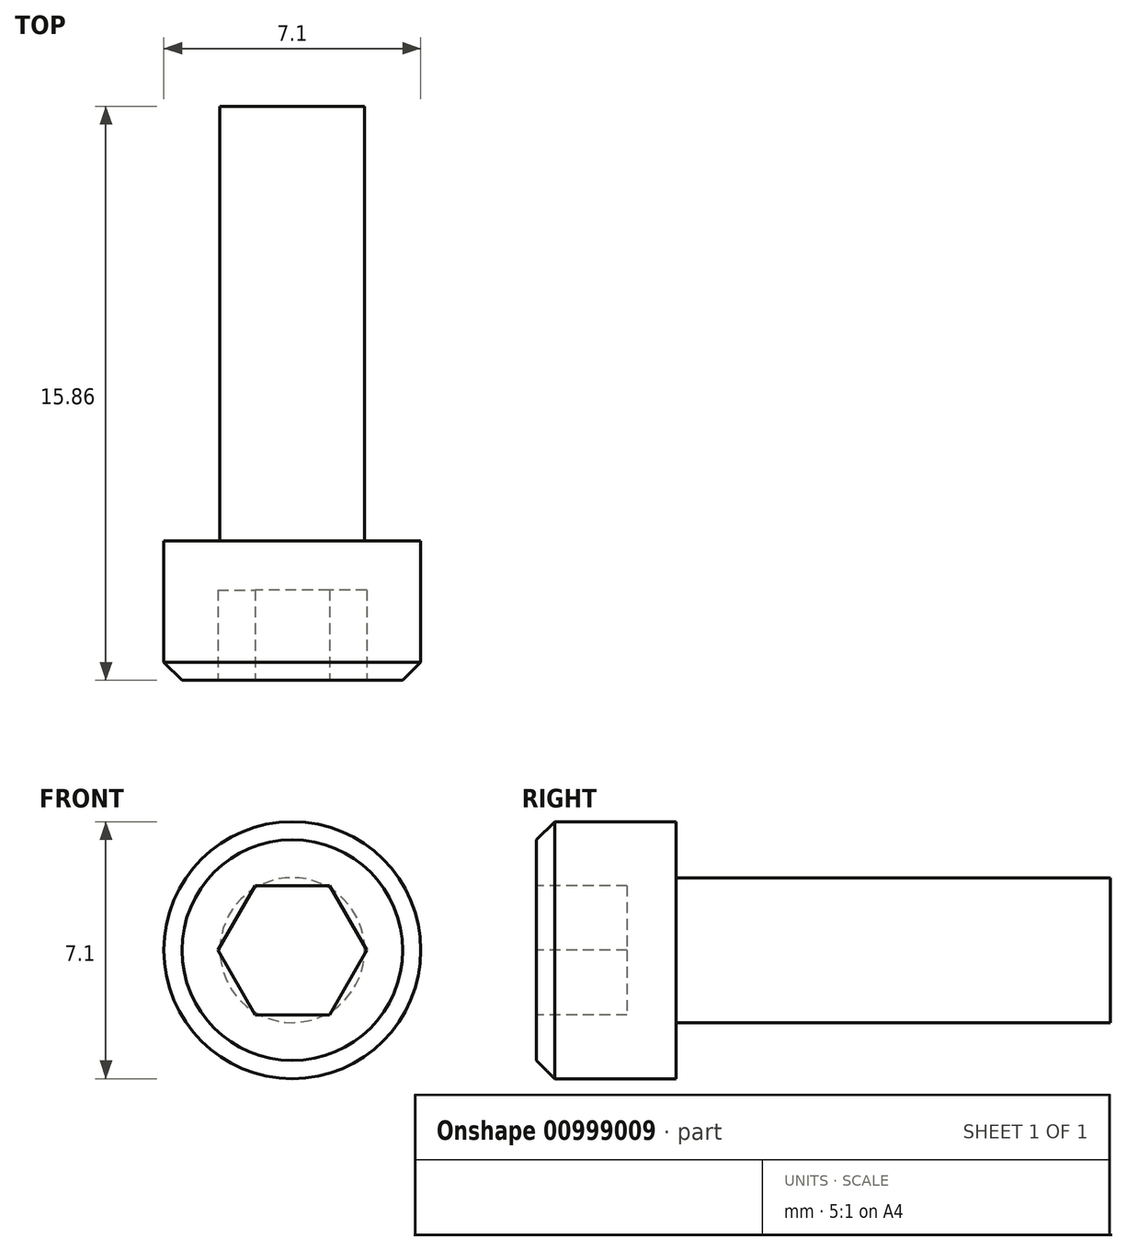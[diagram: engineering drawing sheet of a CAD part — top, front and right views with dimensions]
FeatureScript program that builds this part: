
annotation { "Feature Type Name" : "Feature", "Feature Type Description" : "" }
export const myFeature = defineFeature(function(context is Context, id is Id, definition is map)
    precondition{}
    {
        {
            var Q0;
            Q0=qCreatedBy(makeId("Front.planeOp"),FACE);
            var sketch = newSketch(context, id + "F0", { "sketchPlane" : qUnion([Q0])});
            skCircle(sketch, "E0", {"center": v(0, 0) * mm, "radius": 3.55 * mm});
            skSolve(sketch);
        }
        {
            var Q0;
            Q0=makeQuery(id+"F0.imprint","IMPRINT",FACE,{"disambiguationData":[TD([[makeQuery(id+"F0.imprint","IMPRINT",EDGE,{"derivedFrom":sQuery(id+"F0.wireOp",EDGE,"E0")}),1.0]])]});
            extrude(context, id + "F1", {"entities" : qUnion([Q0]), "depth" : 3.86 * mm, "offsetDistance" : 25 * mm});
        }
        {
            var Q0;
            Q0=makeQuery(id+"F1.opExtrude","CAP_FACE",FACE,{"disambiguationData":[OSD([sQuery(id+"F0.wireOp",EDGE,"E0")])],"isStart":false});
            var sketch = newSketch(context, id + "F2", { "sketchPlane" : qUnion([Q0])});
            skCircle(sketch, "E1.cCircle", {"center": v(0, 0) * mm, "radius": 1.78 * mm, "construction": true});
            skLineSegment(sketch, "E1.0", {"start": v(1.03, -1.78) * mm, "end": v(-1.03, -1.78) * mm});
            skLineSegment(sketch, "E1.1", {"start": v(-1.03, -1.78) * mm, "end": v(-2.06, 0) * mm});
            skLineSegment(sketch, "E1.2", {"start": v(-2.06, 0) * mm, "end": v(-1.03, 1.78) * mm});
            skLineSegment(sketch, "E1.3", {"start": v(-1.03, 1.78) * mm, "end": v(1.03, 1.78) * mm});
            skLineSegment(sketch, "E1.4", {"start": v(1.03, 1.78) * mm, "end": v(2.06, 0) * mm});
            skLineSegment(sketch, "E1.5", {"start": v(2.06, 0) * mm, "end": v(1.03, -1.78) * mm});
            skPoint(sketch, "E1.0.midPoint", {"position": v(0, -1.78) * mm});
            skSolve(sketch);
        }
        {
            var Q0;
            Q0=makeQuery(id+"F2.imprint","IMPRINT",FACE,{"disambiguationData":[TD([[makeQuery(id+"F2.imprint","IMPRINT",EDGE,{"derivedFrom":sQuery(id+"F2.wireOp",EDGE,"E1.0")}),-1.0]])]});
            extrude(context, id + "F3", {"entities" : qUnion([Q0]), "operationType" : NewBodyOperationType.REMOVE, "oppositeDirection" : true, "depth" : 2.5 * mm, "offsetDistance" : 25 * mm});
        }
        {
            var Q0;
            Q0=makeQuery(id+"F1.opExtrude","CAP_FACE",FACE,{"disambiguationData":[OSD([sQuery(id+"F0.wireOp",EDGE,"E0")])],"isStart":true});
            var sketch = newSketch(context, id + "F4", { "sketchPlane" : qUnion([Q0])});
            skCircle(sketch, "E2", {"center": v(0, 0) * mm, "radius": 2 * mm});
            skSolve(sketch);
        }
        {
            var Q0;
            Q0 = qSketchRegion(id + "F4", true);
            extrude(context, id + "F5", {"entities" : qUnion([Q0]), "operationType" : NewBodyOperationType.ADD, "depth" : 12 * mm, "offsetDistance" : 25 * mm});
        }
        {
            var Q0;
            Q0=makeQuery(id+"F1.opExtrude","CAP_EDGE",EDGE,{"disambiguationData":[OSD([sQuery(id+"F0.wireOp",EDGE,"E0")])],"isStart":false});
            chamfer(context, id + "F6", {"entities" : qUnion([Q0]), "width" : .5 * mm, "tangentPropagation" : true});
        }
    });
